# Revit family: Filtration Cabinet_OPEN_3-2-2020
name_source: partatom
category: Mechanical Equipment
revit_build: Autodesk Revit 2017 (Build: 20190508_0315(x64)
units: mm (PartAtom-declared; Revit-internal decimal feet)

## family parameters
Always vertical = Yes
Cut with Voids When Loaded = No
Part Type = Normal
Room Calculation Point = No
Round Connector Dimension = Use Diameter
Shared = No
Work Plane-Based = No

## types (5) — shared parameters
120 VAC / 1 Phase / 60 Hz = Yes
Clearance Material = Clearance Material
Cutting Zone Material = Cutting Zone Material
Depth = 1' - 0"
Description = Automatic Fuel Oil Filtration Cabinet
Height = 5' - 8"
Manufacturer = Preferred Utilities MFG
Outlet Diameter = 0' - 1 1/2"
Outlet Radius = 0' - 0 3/4"
URL = www.preferred-mfg.com
Width = 4' - 0"

## per-type parameters (varying)
| type | 1/2_HP | 1/3_HP | 1/4_HP | 3/4 HP | GPH_Oil_2 | Inlet Diameter | Inlet Radius | PSI | RPM |
| PF-501 | No | No | Yes | No | 180 | 0' - 0 3/4" | 0' - 0 3/8" | 15 | 1725 |
| PF-502 | No | Yes | No | No | 480 | 0' - 0 3/4" | 0' - 0 3/8" | 15 | 3450 |
| PF-503 | Yes | No | No | No | 600 | 0' - 0 3/4" | 0' - 0 3/8" | 30 | 1725 |
| PF-504 | No | No | No | Yes | 900 | 0' - 1 1/2" | 0' - 0 3/4" | 30 | 1725 |
| PF-505 | No | No | No | Yes | 1200 | 0' - 1 1/2" | 0' - 0 3/4" | 25 | 1725 |

note: column(s) folded — value = type name in every type: Model

## geometry (parser evidence)
native form markers: Sweep x2
no freeform markers — native parametric forms only
